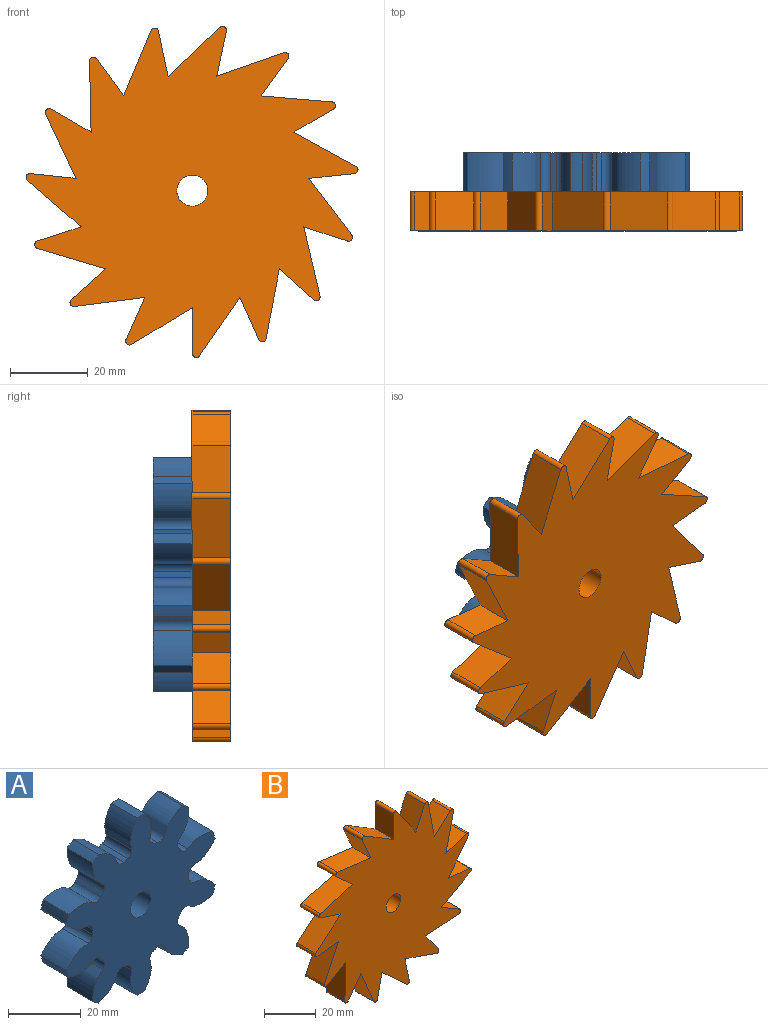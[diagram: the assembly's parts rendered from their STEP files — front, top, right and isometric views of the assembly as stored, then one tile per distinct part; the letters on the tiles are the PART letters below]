
ASSEMBLY  parts=2 mates=1
PART A: 63 faces, bbox 58x10x60.1 mm
  f0: cylinder r=30mm len=10mm, axis (0,1,0), area 29.4mm2, adj f9,f11,f52,f59
  f1: cylinder r=30mm len=10mm, axis (0,1,0), area 29.4mm2, adj f9,f11,f12,f54
  f2: cylinder r=30mm len=10mm, axis (0,1,0), area 29.4mm2, adj f9,f11,f42,f49
  f3: cylinder r=30mm len=10mm, axis (0,1,0), area 29.4mm2, adj f9,f11,f44,f57
  f4: cylinder r=30mm len=10mm, axis (0,1,0), area 29.4mm2, adj f9,f11,f32,f39
  f5: cylinder r=30mm len=10mm, axis (0,1,0), area 29.4mm2, adj f9,f11,f27,f34
  f6: cylinder r=30mm len=10mm, axis (0,1,0), area 29.4mm2, adj f9,f11,f22,f29
  f7: cylinder r=30mm len=10mm, axis (0,1,0), area 29.4mm2, adj f9,f11,f24,f47
  f8: cylinder r=30mm len=10mm, axis (0,1,0), area 29.4mm2, adj f9,f11,f19,f37
  f9: plane 60.1x58.03mm, normal (0,-1,0), area 1827.9mm2, adj f0,f1,f2,f3,f4,f5,f6,f7
  f10: cylinder r=30mm len=10mm, axis (0,1,0), area 29.4mm2, adj f9,f11,f14,f17
  f11: plane 60.1x58.03mm, normal (0,1,0), area 1827.9mm2, adj f0,f1,f2,f3,f4,f5,f6,f7
  f12: extruded ~10x8.45mm, area 101.4mm2, adj f1,f9,f11,f15
  f13: cylinder r=18.75mm len=10mm, axis (0,1,0), area 16.1mm2, adj f9,f11,f15,f16
  f14: extruded ~10x8.45mm, area 101.4mm2, adj f9,f10,f11,f16
  f15: cylinder r=2.06mm len=10mm, axis (0,1,0), area 30.3mm2, adj f9,f11,f12,f13
  f16: cylinder r=2.06mm len=10mm, axis (0,1,0), area 30.3mm2, adj f9,f11,f13,f14
  f17: extruded ~10x9.74mm, area 101.4mm2, adj f9,f10,f11,f20
  f18: cylinder r=18.75mm len=10mm, axis (0,1,0), area 16.1mm2, adj f9,f11,f20,f21
  f19: extruded ~10x8.96mm, area 101.4mm2, adj f8,f9,f11,f21
  f20: cylinder r=2.06mm len=10mm, axis (0,1,0), area 30.3mm2, adj f9,f11,f17,f18
  f21: cylinder r=2.06mm len=10mm, axis (0,1,0), area 30.3mm2, adj f9,f11,f18,f19
  f22: extruded ~10x8.45mm, area 101.4mm2, adj f6,f9,f11,f25
  f23: cylinder r=18.75mm len=10mm, axis (0,1,0), area 16.1mm2, adj f9,f11,f25,f26
  f24: extruded ~10x8.45mm, area 101.4mm2, adj f7,f9,f11,f26
  f25: cylinder r=2.06mm len=10mm, axis (0,1,0), area 30.3mm2, adj f9,f11,f22,f23
  f26: cylinder r=2.06mm len=10mm, axis (0,1,0), area 30.3mm2, adj f9,f11,f23,f24
  f27: extruded ~10x8.96mm, area 101.4mm2, adj f5,f9,f11,f30
  f28: cylinder r=18.75mm len=10mm, axis (0,1,0), area 16.1mm2, adj f9,f11,f30,f31
  f29: extruded ~10x9.74mm, area 101.4mm2, adj f6,f9,f11,f31
  f30: cylinder r=2.06mm len=10mm, axis (0,1,0), area 30.3mm2, adj f9,f11,f27,f28
  f31: cylinder r=2.06mm len=10mm, axis (0,1,0), area 30.3mm2, adj f9,f11,f28,f29
  f32: extruded ~10x9.56mm, area 101.4mm2, adj f4,f9,f11,f35
  f33: cylinder r=18.75mm len=10mm, axis (0,1,0), area 16.1mm2, adj f9,f11,f35,f36
  f34: extruded ~10x7.3mm, area 101.4mm2, adj f5,f9,f11,f36
  f35: cylinder r=2.06mm len=10mm, axis (0,1,0), area 30.3mm2, adj f9,f11,f32,f33
  f36: cylinder r=2.06mm len=10mm, axis (0,1,0), area 30.3mm2, adj f9,f11,f33,f34
  f37: extruded ~10x7.3mm, area 101.4mm2, adj f8,f9,f11,f40
  f38: cylinder r=18.75mm len=10mm, axis (0,1,0), area 16.1mm2, adj f9,f11,f40,f41
  f39: extruded ~10x9.56mm, area 101.4mm2, adj f4,f9,f11,f41
  f40: cylinder r=2.06mm len=10mm, axis (0,1,0), area 30.3mm2, adj f9,f11,f37,f38
  f41: cylinder r=2.06mm len=10mm, axis (0,1,0), area 30.3mm2, adj f9,f11,f38,f39
  f42: extruded ~10x7.3mm, area 101.4mm2, adj f2,f9,f11,f45
  f43: cylinder r=18.75mm len=10mm, axis (0,1,0), area 16.1mm2, adj f9,f11,f45,f46
  f44: extruded ~10x9.56mm, area 101.4mm2, adj f3,f9,f11,f46
  f45: cylinder r=2.06mm len=10mm, axis (0,1,0), area 30.3mm2, adj f9,f11,f42,f43
  f46: cylinder r=2.06mm len=10mm, axis (0,1,0), area 30.3mm2, adj f9,f11,f43,f44
  f47: extruded ~10x9.74mm, area 101.4mm2, adj f7,f9,f11,f50
  f48: cylinder r=18.75mm len=10mm, axis (0,1,0), area 16.1mm2, adj f9,f11,f50,f51
  f49: extruded ~10x8.96mm, area 101.4mm2, adj f2,f9,f11,f51
  f50: cylinder r=2.06mm len=10mm, axis (0,1,0), area 30.3mm2, adj f9,f11,f47,f48
  f51: cylinder r=2.06mm len=10mm, axis (0,1,0), area 30.3mm2, adj f9,f11,f48,f49
  f52: extruded ~10x8.96mm, area 101.4mm2, adj f0,f9,f11,f55
  f53: cylinder r=18.75mm len=10mm, axis (0,1,0), area 16.1mm2, adj f9,f11,f55,f56
  f54: extruded ~10x9.74mm, area 101.4mm2, adj f1,f9,f11,f56
  f55: cylinder r=2.06mm len=10mm, axis (0,1,0), area 30.3mm2, adj f9,f11,f52,f53
  f56: cylinder r=2.06mm len=10mm, axis (0,1,0), area 30.3mm2, adj f9,f11,f53,f54
  f57: extruded ~10x9.56mm, area 101.4mm2, adj f3,f9,f11,f60
  f58: cylinder r=18.75mm len=10mm, axis (0,1,0), area 16.1mm2, adj f9,f11,f60,f61
  f59: extruded ~10x7.3mm, area 101.4mm2, adj f0,f9,f11,f61
  f60: cylinder r=2.06mm len=10mm, axis (0,1,0), area 30.3mm2, adj f9,f11,f57,f58
  f61: cylinder r=2.06mm len=10mm, axis (0,1,0), area 30.3mm2, adj f9,f11,f58,f59
  f62: cylinder r=4mm len=10mm, axis (0,-1,0), area 251.3mm2, adj f9,f11
PART B: 48 faces, bbox 85.1x10x84.9 mm
  f0: plane 18.07x10mm, normal (0.13,0,0.99), area 182.1mm2, adj f2,f3,f4,f6
  f1: plane 10x8.77mm, normal (-0.67,0,-0.74), area 118mm2, adj f2,f3,f4,f44
  f2: plane 85.15x84.9mm, normal (0,-1,0), area 4039mm2, adj f0,f1,f4,f5,f6,f7,f8,f9
  f3: plane 85.15x84.9mm, normal (0,1,0), area 4039mm2, adj f0,f1,f4,f5,f6,f7,f8,f9
  f4: cylinder r=1mm len=10mm, axis (0,1,0), area 25.4mm2, adj f0,f1,f2,f3
  f5: plane 15.57x10mm, normal (0.52,0,0.85), area 182.1mm2, adj f2,f3,f7,f9
  f6: plane 10.78x10mm, normal (-0.91,0,-0.41), area 118mm2, adj f0,f2,f3,f7
  f7: cylinder r=1mm len=10mm, axis (0,1,0), area 25.4mm2, adj f2,f3,f5,f6
  f8: plane 14.97x10.38mm, normal (0.82,0,0.57), area 182.1mm2, adj f2,f3,f10,f12
  f9: plane 11.8x10mm, normal (-1,0,0), area 118mm2, adj f2,f3,f5,f10
  f10: cylinder r=1mm len=10mm, axis (0,1,0), area 25.4mm2, adj f2,f3,f8,f9
  f11: plane 17.9x10mm, normal (0.98,0,0.19), area 182.1mm2, adj f2,f3,f13,f15
  f12: plane 10.78x10mm, normal (-0.91,0,0.41), area 118mm2, adj f2,f3,f8,f13
  f13: cylinder r=1mm len=10mm, axis (0,1,0), area 25.4mm2, adj f2,f3,f11,f12
  f14: plane 17.73x10mm, normal (0.97,0,-0.23), area 182.1mm2, adj f2,f3,f16,f18
  f15: plane 10x8.77mm, normal (-0.67,0,0.74), area 118mm2, adj f2,f3,f11,f16
  f16: cylinder r=1mm len=10mm, axis (0,1,0), area 25.4mm2, adj f2,f3,f14,f15
  f17: plane 14.5x11.03mm, normal (0.8,0,-0.61), area 182.1mm2, adj f2,f3,f19,f21
  f18: plane 11.23x10mm, normal (-0.31,0,0.95), area 118mm2, adj f2,f3,f14,f19
  f19: cylinder r=1mm len=10mm, axis (0,1,0), area 25.4mm2, adj f2,f3,f17,f18
  f20: plane 15.97x10mm, normal (0.48,0,-0.88), area 182.1mm2, adj f2,f3,f22,f24
  f21: plane 11.74x10mm, normal (0.1,0,0.99), area 118mm2, adj f2,f3,f17,f22
  f22: cylinder r=1mm len=10mm, axis (0,1,0), area 25.4mm2, adj f2,f3,f20,f21
  f23: plane 18.15x10mm, normal (0.08,0,-1), area 182.1mm2, adj f2,f3,f25,f27
  f24: plane 10.22x10mm, normal (0.5,0,0.87), area 118mm2, adj f2,f3,f20,f25
  f25: cylinder r=1mm len=10mm, axis (0,1,0), area 25.4mm2, adj f2,f3,f23,f24
  f26: plane 17.2x10mm, normal (-0.33,0,-0.94), area 182.1mm2, adj f2,f3,f28,f30
  f27: plane 10x9.55mm, normal (0.81,0,0.59), area 118mm2, adj f2,f3,f23,f28
  f28: cylinder r=1mm len=10mm, axis (0,1,0), area 25.4mm2, adj f2,f3,f26,f27
  f29: plane 13.27x12.48mm, normal (-0.69,0,-0.73), area 182.1mm2, adj f2,f3,f31,f33
  f30: plane 11.55x10mm, normal (0.98,0,0.21), area 118mm2, adj f2,f3,f26,f31
  f31: cylinder r=1mm len=10mm, axis (0,1,0), area 25.4mm2, adj f2,f3,f29,f30
  f32: plane 16.8x10mm, normal (-0.92,0,-0.39), area 182.1mm2, adj f2,f3,f34,f36
  f33: plane 11.55x10mm, normal (0.98,0,-0.21), area 118mm2, adj f2,f3,f29,f34
  f34: cylinder r=1mm len=10mm, axis (0,1,0), area 25.4mm2, adj f2,f3,f32,f33
  f35: plane 18.21x10mm, normal (-1,0,0.02), area 182.1mm2, adj f2,f3,f37,f39
  f36: plane 10x9.55mm, normal (0.81,0,-0.59), area 118mm2, adj f2,f3,f32,f37
  f37: cylinder r=1mm len=10mm, axis (0,1,0), area 25.4mm2, adj f2,f3,f35,f36
  f38: plane 16.47x10mm, normal (-0.9,0,0.43), area 182.1mm2, adj f2,f3,f40,f42
  f39: plane 10.22x10mm, normal (0.5,0,-0.87), area 118mm2, adj f2,f3,f35,f40
  f40: cylinder r=1mm len=10mm, axis (0,1,0), area 25.4mm2, adj f2,f3,f38,f39
  f41: plane 13.8x11.89mm, normal (-0.65,0,0.76), area 182.1mm2, adj f2,f3,f43,f45
  f42: plane 11.74x10mm, normal (0.1,0,-0.99), area 118mm2, adj f2,f3,f38,f43
  f43: cylinder r=1mm len=10mm, axis (0,1,0), area 25.4mm2, adj f2,f3,f41,f42
  f44: plane 17.44x10mm, normal (-0.29,0,0.96), area 182.1mm2, adj f1,f2,f3,f46
  f45: plane 11.23x10mm, normal (-0.31,0,-0.95), area 118mm2, adj f2,f3,f41,f46
  f46: cylinder r=1mm len=10mm, axis (0,1,0), area 25.4mm2, adj f2,f3,f44,f45
  f47: cylinder r=4mm len=10mm, axis (0,1,0), area 251.3mm2, adj f2,f3
PLACE A rot(axis=(0,0,1),0deg) t=(-37.12,-23.54,-10.66)mm
PLACE B rot(axis=(1,0,0),180deg) t=(-37.12,-43.54,-10.66)mm
MATE fastened A.f62 <-> B.f47  axis (0,-1,0) through (-37.12,-33.54,-10.66)mm
